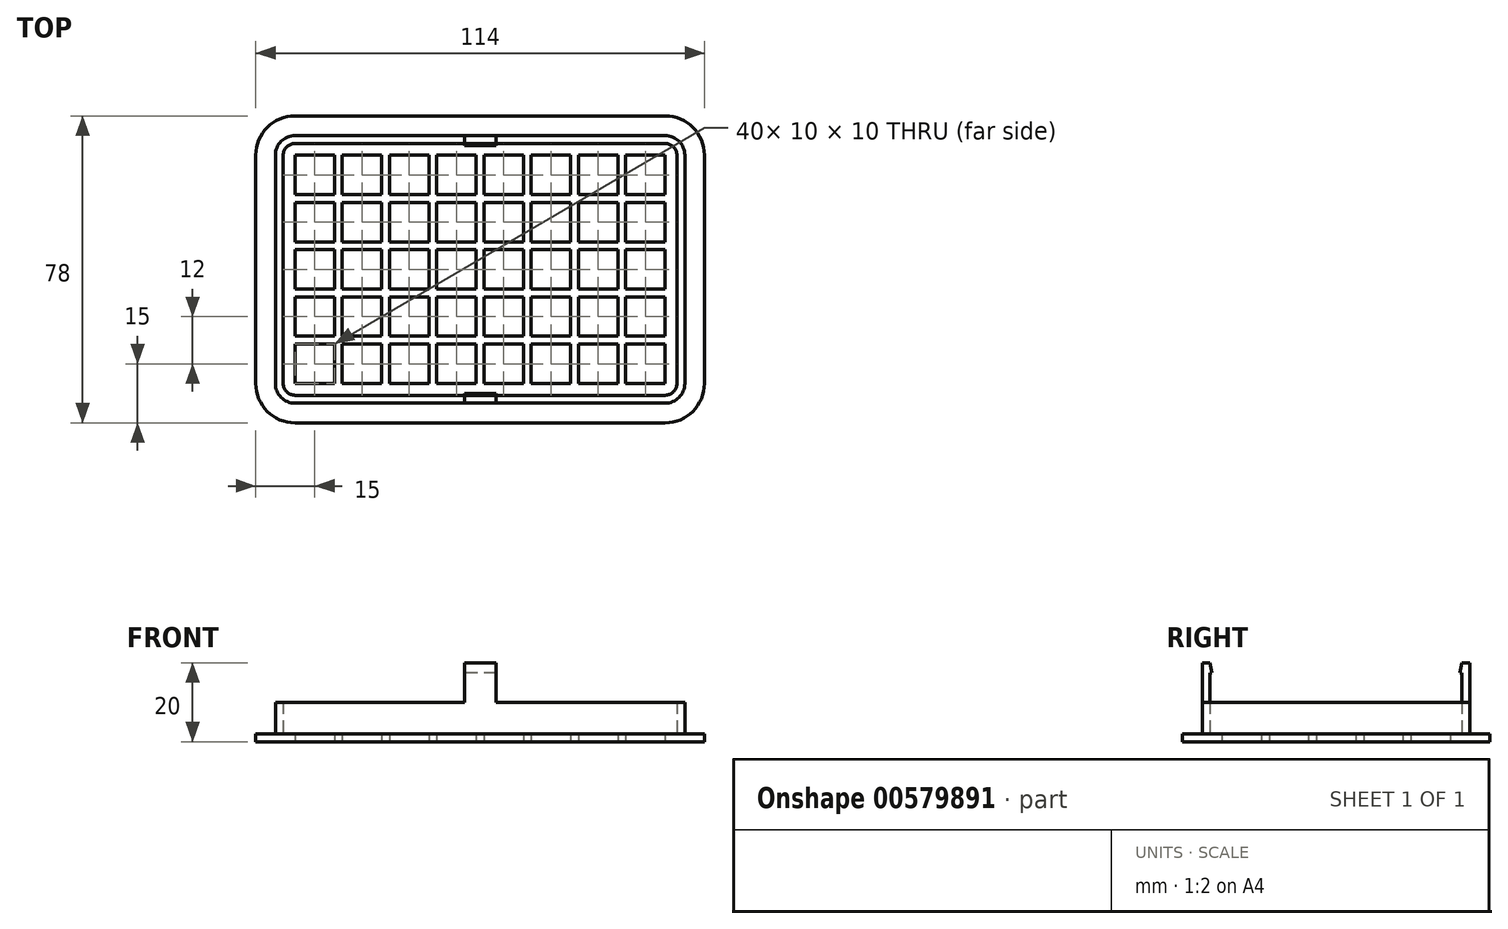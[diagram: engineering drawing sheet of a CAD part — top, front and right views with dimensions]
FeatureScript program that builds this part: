
annotation { "Feature Type Name" : "Feature", "Feature Type Description" : "" }
export const myFeature = defineFeature(function(context is Context, id is Id, definition is map)
    precondition{}
    {
        {
            var Q0;
            Q0=qCreatedBy(makeId("Top.planeOp"),FACE);
            var sketch = newSketch(context, id + "F0", { "sketchPlane" : qUnion([Q0])});
            skLineSegment(sketch, "E0.bottom", {"start": v(10, 0) * mm, "end": v(104, 0) * mm});
            skLineSegment(sketch, "E0.top", {"start": v(10, 78) * mm, "end": v(104, 78) * mm});
            skLineSegment(sketch, "E0.left", {"start": v(0, 10) * mm, "end": v(0, 68) * mm});
            skLineSegment(sketch, "E0.right", {"start": v(114, 10) * mm, "end": v(114, 68) * mm});
            skPoint(sketch, "E1.visualSharp", {"position": v(0, 78) * mm});
            skArc(sketch, "E1.filletArc", {"start": v(10, 78) * mm, "mid": v(2.93, 75.07) * mm, "end": v(0, 68) * mm});
            skPoint(sketch, "E2.visualSharp", {"position": v(114, 78) * mm});
            skArc(sketch, "E2.filletArc", {"start": v(114, 68) * mm, "mid": v(111.07, 75.07) * mm, "end": v(104, 78) * mm});
            skPoint(sketch, "E3.visualSharp", {"position": v(114, 0) * mm});
            skArc(sketch, "E3.filletArc", {"start": v(104, 0) * mm, "mid": v(111.07, 2.93) * mm, "end": v(114, 10) * mm});
            skPoint(sketch, "E4.visualSharp", {"position": v(0, 0) * mm});
            skArc(sketch, "E4.filletArc", {"start": v(0, 10) * mm, "mid": v(2.93, 2.93) * mm, "end": v(10, 0) * mm});
            skArc(sketch, "E5.0", {"start": v(5, 10) * mm, "mid": v(6.46, 6.46) * mm, "end": v(10, 5) * mm});
            skLineSegment(sketch, "E5.1", {"start": v(5, 10) * mm, "end": v(5, 68) * mm});
            skLineSegment(sketch, "E5.2", {"start": v(10, 5) * mm, "end": v(104, 5) * mm});
            skArc(sketch, "E5.3", {"start": v(10, 73) * mm, "mid": v(6.46, 71.54) * mm, "end": v(5, 68) * mm});
            skArc(sketch, "E5.4", {"start": v(104, 5) * mm, "mid": v(107.54, 6.46) * mm, "end": v(109, 10) * mm});
            skLineSegment(sketch, "E5.5", {"start": v(109, 10) * mm, "end": v(109, 68) * mm});
            skArc(sketch, "E5.6", {"start": v(109, 68) * mm, "mid": v(107.54, 71.54) * mm, "end": v(104, 73) * mm});
            skLineSegment(sketch, "E5.7", {"start": v(10, 73) * mm, "end": v(104, 73) * mm});
            skArc(sketch, "E6.0", {"start": v(7, 10) * mm, "mid": v(7.88, 7.88) * mm, "end": v(10, 7) * mm});
            skLineSegment(sketch, "E6.1", {"start": v(7, 10) * mm, "end": v(7, 68) * mm});
            skLineSegment(sketch, "E6.2", {"start": v(10, 7) * mm, "end": v(104, 7) * mm});
            skArc(sketch, "E6.3", {"start": v(10, 71) * mm, "mid": v(7.88, 70.12) * mm, "end": v(7, 68) * mm});
            skArc(sketch, "E6.4", {"start": v(104, 7) * mm, "mid": v(106.12, 7.88) * mm, "end": v(107, 10) * mm});
            skLineSegment(sketch, "E6.5", {"start": v(107, 10) * mm, "end": v(107, 68) * mm});
            skArc(sketch, "E6.6", {"start": v(107, 68) * mm, "mid": v(106.12, 70.12) * mm, "end": v(104, 71) * mm});
            skLineSegment(sketch, "E6.7", {"start": v(10, 71) * mm, "end": v(104, 71) * mm});
            skLineSegment(sketch, "E7.bottom", {"start": v(10, 68) * mm, "end": v(20, 68) * mm});
            skLineSegment(sketch, "E7.top", {"start": v(10, 58) * mm, "end": v(20, 58) * mm});
            skLineSegment(sketch, "E7.left", {"start": v(10, 68) * mm, "end": v(10, 58) * mm});
            skLineSegment(sketch, "E7.right", {"start": v(20, 68) * mm, "end": v(20, 58) * mm});
            skLineSegment(sketch, "E8.0.1.0", {"start": v(10, 46) * mm, "end": v(20, 46) * mm});
            skLineSegment(sketch, "E8.0.1.1", {"start": v(20, 56) * mm, "end": v(20, 46) * mm});
            skLineSegment(sketch, "E8.0.1.2", {"start": v(10, 56) * mm, "end": v(20, 56) * mm});
            skLineSegment(sketch, "E8.0.1.3", {"start": v(10, 56) * mm, "end": v(10, 46) * mm});
            skLineSegment(sketch, "E8.0.2.0", {"start": v(10, 34) * mm, "end": v(20, 34) * mm});
            skLineSegment(sketch, "E8.0.2.1", {"start": v(20, 44) * mm, "end": v(20, 34) * mm});
            skLineSegment(sketch, "E8.0.2.2", {"start": v(10, 44) * mm, "end": v(20, 44) * mm});
            skLineSegment(sketch, "E8.0.2.3", {"start": v(10, 44) * mm, "end": v(10, 34) * mm});
            skLineSegment(sketch, "E8.0.3.0", {"start": v(10, 22) * mm, "end": v(20, 22) * mm});
            skLineSegment(sketch, "E8.0.3.1", {"start": v(20, 32) * mm, "end": v(20, 22) * mm});
            skLineSegment(sketch, "E8.0.3.2", {"start": v(10, 32) * mm, "end": v(20, 32) * mm});
            skLineSegment(sketch, "E8.0.3.3", {"start": v(10, 32) * mm, "end": v(10, 22) * mm});
            skLineSegment(sketch, "E8.0.4.0", {"start": v(10, 10) * mm, "end": v(20, 10) * mm});
            skLineSegment(sketch, "E8.0.4.1", {"start": v(20, 20) * mm, "end": v(20, 10) * mm});
            skLineSegment(sketch, "E8.0.4.2", {"start": v(10, 20) * mm, "end": v(20, 20) * mm});
            skLineSegment(sketch, "E8.0.4.3", {"start": v(10, 20) * mm, "end": v(10, 10) * mm});
            skLineSegment(sketch, "E8.1.0.0", {"start": v(22, 58) * mm, "end": v(32, 58) * mm});
            skLineSegment(sketch, "E8.1.0.1", {"start": v(32, 68) * mm, "end": v(32, 58) * mm});
            skLineSegment(sketch, "E8.1.0.2", {"start": v(22, 68) * mm, "end": v(32, 68) * mm});
            skLineSegment(sketch, "E8.1.0.3", {"start": v(22, 68) * mm, "end": v(22, 58) * mm});
            skLineSegment(sketch, "E8.1.1.0", {"start": v(22, 46) * mm, "end": v(32, 46) * mm});
            skLineSegment(sketch, "E8.1.1.1", {"start": v(32, 56) * mm, "end": v(32, 46) * mm});
            skLineSegment(sketch, "E8.1.1.2", {"start": v(22, 56) * mm, "end": v(32, 56) * mm});
            skLineSegment(sketch, "E8.1.1.3", {"start": v(22, 56) * mm, "end": v(22, 46) * mm});
            skLineSegment(sketch, "E8.1.2.0", {"start": v(22, 34) * mm, "end": v(32, 34) * mm});
            skLineSegment(sketch, "E8.1.2.1", {"start": v(32, 44) * mm, "end": v(32, 34) * mm});
            skLineSegment(sketch, "E8.1.2.2", {"start": v(22, 44) * mm, "end": v(32, 44) * mm});
            skLineSegment(sketch, "E8.1.2.3", {"start": v(22, 44) * mm, "end": v(22, 34) * mm});
            skLineSegment(sketch, "E8.1.3.0", {"start": v(22, 22) * mm, "end": v(32, 22) * mm});
            skLineSegment(sketch, "E8.1.3.1", {"start": v(32, 32) * mm, "end": v(32, 22) * mm});
            skLineSegment(sketch, "E8.1.3.2", {"start": v(22, 32) * mm, "end": v(32, 32) * mm});
            skLineSegment(sketch, "E8.1.3.3", {"start": v(22, 32) * mm, "end": v(22, 22) * mm});
            skLineSegment(sketch, "E8.1.4.0", {"start": v(22, 10) * mm, "end": v(32, 10) * mm});
            skLineSegment(sketch, "E8.1.4.1", {"start": v(32, 20) * mm, "end": v(32, 10) * mm});
            skLineSegment(sketch, "E8.1.4.2", {"start": v(22, 20) * mm, "end": v(32, 20) * mm});
            skLineSegment(sketch, "E8.1.4.3", {"start": v(22, 20) * mm, "end": v(22, 10) * mm});
            skLineSegment(sketch, "E8.2.0.0", {"start": v(34, 58) * mm, "end": v(44, 58) * mm});
            skLineSegment(sketch, "E8.2.0.1", {"start": v(44, 68) * mm, "end": v(44, 58) * mm});
            skLineSegment(sketch, "E8.2.0.2", {"start": v(34, 68) * mm, "end": v(44, 68) * mm});
            skLineSegment(sketch, "E8.2.0.3", {"start": v(34, 68) * mm, "end": v(34, 58) * mm});
            skLineSegment(sketch, "E8.2.1.0", {"start": v(34, 46) * mm, "end": v(44, 46) * mm});
            skLineSegment(sketch, "E8.2.1.1", {"start": v(44, 56) * mm, "end": v(44, 46) * mm});
            skLineSegment(sketch, "E8.2.1.2", {"start": v(34, 56) * mm, "end": v(44, 56) * mm});
            skLineSegment(sketch, "E8.2.1.3", {"start": v(34, 56) * mm, "end": v(34, 46) * mm});
            skLineSegment(sketch, "E8.2.2.0", {"start": v(34, 34) * mm, "end": v(44, 34) * mm});
            skLineSegment(sketch, "E8.2.2.1", {"start": v(44, 44) * mm, "end": v(44, 34) * mm});
            skLineSegment(sketch, "E8.2.2.2", {"start": v(34, 44) * mm, "end": v(44, 44) * mm});
            skLineSegment(sketch, "E8.2.2.3", {"start": v(34, 44) * mm, "end": v(34, 34) * mm});
            skLineSegment(sketch, "E8.2.3.0", {"start": v(34, 22) * mm, "end": v(44, 22) * mm});
            skLineSegment(sketch, "E8.2.3.1", {"start": v(44, 32) * mm, "end": v(44, 22) * mm});
            skLineSegment(sketch, "E8.2.3.2", {"start": v(34, 32) * mm, "end": v(44, 32) * mm});
            skLineSegment(sketch, "E8.2.3.3", {"start": v(34, 32) * mm, "end": v(34, 22) * mm});
            skLineSegment(sketch, "E8.2.4.0", {"start": v(34, 10) * mm, "end": v(44, 10) * mm});
            skLineSegment(sketch, "E8.2.4.1", {"start": v(44, 20) * mm, "end": v(44, 10) * mm});
            skLineSegment(sketch, "E8.2.4.2", {"start": v(34, 20) * mm, "end": v(44, 20) * mm});
            skLineSegment(sketch, "E8.2.4.3", {"start": v(34, 20) * mm, "end": v(34, 10) * mm});
            skLineSegment(sketch, "E8.3.0.0", {"start": v(46, 58) * mm, "end": v(56, 58) * mm});
            skLineSegment(sketch, "E8.3.0.1", {"start": v(56, 68) * mm, "end": v(56, 58) * mm});
            skLineSegment(sketch, "E8.3.0.2", {"start": v(46, 68) * mm, "end": v(56, 68) * mm});
            skLineSegment(sketch, "E8.3.0.3", {"start": v(46, 68) * mm, "end": v(46, 58) * mm});
            skLineSegment(sketch, "E8.3.1.0", {"start": v(46, 46) * mm, "end": v(56, 46) * mm});
            skLineSegment(sketch, "E8.3.1.1", {"start": v(56, 56) * mm, "end": v(56, 46) * mm});
            skLineSegment(sketch, "E8.3.1.2", {"start": v(46, 56) * mm, "end": v(56, 56) * mm});
            skLineSegment(sketch, "E8.3.1.3", {"start": v(46, 56) * mm, "end": v(46, 46) * mm});
            skLineSegment(sketch, "E8.3.2.0", {"start": v(46, 34) * mm, "end": v(56, 34) * mm});
            skLineSegment(sketch, "E8.3.2.1", {"start": v(56, 44) * mm, "end": v(56, 34) * mm});
            skLineSegment(sketch, "E8.3.2.2", {"start": v(46, 44) * mm, "end": v(56, 44) * mm});
            skLineSegment(sketch, "E8.3.2.3", {"start": v(46, 44) * mm, "end": v(46, 34) * mm});
            skLineSegment(sketch, "E8.3.3.0", {"start": v(46, 22) * mm, "end": v(56, 22) * mm});
            skLineSegment(sketch, "E8.3.3.1", {"start": v(56, 32) * mm, "end": v(56, 22) * mm});
            skLineSegment(sketch, "E8.3.3.2", {"start": v(46, 32) * mm, "end": v(56, 32) * mm});
            skLineSegment(sketch, "E8.3.3.3", {"start": v(46, 32) * mm, "end": v(46, 22) * mm});
            skLineSegment(sketch, "E8.3.4.0", {"start": v(46, 10) * mm, "end": v(56, 10) * mm});
            skLineSegment(sketch, "E8.3.4.1", {"start": v(56, 20) * mm, "end": v(56, 10) * mm});
            skLineSegment(sketch, "E8.3.4.2", {"start": v(46, 20) * mm, "end": v(56, 20) * mm});
            skLineSegment(sketch, "E8.3.4.3", {"start": v(46, 20) * mm, "end": v(46, 10) * mm});
            skLineSegment(sketch, "E8.4.0.0", {"start": v(58, 58) * mm, "end": v(68, 58) * mm});
            skLineSegment(sketch, "E8.4.0.1", {"start": v(68, 68) * mm, "end": v(68, 58) * mm});
            skLineSegment(sketch, "E8.4.0.2", {"start": v(58, 68) * mm, "end": v(68, 68) * mm});
            skLineSegment(sketch, "E8.4.0.3", {"start": v(58, 68) * mm, "end": v(58, 58) * mm});
            skLineSegment(sketch, "E8.4.1.0", {"start": v(58, 46) * mm, "end": v(68, 46) * mm});
            skLineSegment(sketch, "E8.4.1.1", {"start": v(68, 56) * mm, "end": v(68, 46) * mm});
            skLineSegment(sketch, "E8.4.1.2", {"start": v(58, 56) * mm, "end": v(68, 56) * mm});
            skLineSegment(sketch, "E8.4.1.3", {"start": v(58, 56) * mm, "end": v(58, 46) * mm});
            skLineSegment(sketch, "E8.4.2.0", {"start": v(58, 34) * mm, "end": v(68, 34) * mm});
            skLineSegment(sketch, "E8.4.2.1", {"start": v(68, 44) * mm, "end": v(68, 34) * mm});
            skLineSegment(sketch, "E8.4.2.2", {"start": v(58, 44) * mm, "end": v(68, 44) * mm});
            skLineSegment(sketch, "E8.4.2.3", {"start": v(58, 44) * mm, "end": v(58, 34) * mm});
            skLineSegment(sketch, "E8.4.3.0", {"start": v(58, 22) * mm, "end": v(68, 22) * mm});
            skLineSegment(sketch, "E8.4.3.1", {"start": v(68, 32) * mm, "end": v(68, 22) * mm});
            skLineSegment(sketch, "E8.4.3.2", {"start": v(58, 32) * mm, "end": v(68, 32) * mm});
            skLineSegment(sketch, "E8.4.3.3", {"start": v(58, 32) * mm, "end": v(58, 22) * mm});
            skLineSegment(sketch, "E8.4.4.0", {"start": v(58, 10) * mm, "end": v(68, 10) * mm});
            skLineSegment(sketch, "E8.4.4.1", {"start": v(68, 20) * mm, "end": v(68, 10) * mm});
            skLineSegment(sketch, "E8.4.4.2", {"start": v(58, 20) * mm, "end": v(68, 20) * mm});
            skLineSegment(sketch, "E8.4.4.3", {"start": v(58, 20) * mm, "end": v(58, 10) * mm});
            skLineSegment(sketch, "E8.5.0.0", {"start": v(70, 58) * mm, "end": v(80, 58) * mm});
            skLineSegment(sketch, "E8.5.0.1", {"start": v(80, 68) * mm, "end": v(80, 58) * mm});
            skLineSegment(sketch, "E8.5.0.2", {"start": v(70, 68) * mm, "end": v(80, 68) * mm});
            skLineSegment(sketch, "E8.5.0.3", {"start": v(70, 68) * mm, "end": v(70, 58) * mm});
            skLineSegment(sketch, "E8.5.1.0", {"start": v(70, 46) * mm, "end": v(80, 46) * mm});
            skLineSegment(sketch, "E8.5.1.1", {"start": v(80, 56) * mm, "end": v(80, 46) * mm});
            skLineSegment(sketch, "E8.5.1.2", {"start": v(70, 56) * mm, "end": v(80, 56) * mm});
            skLineSegment(sketch, "E8.5.1.3", {"start": v(70, 56) * mm, "end": v(70, 46) * mm});
            skLineSegment(sketch, "E8.5.2.0", {"start": v(70, 34) * mm, "end": v(80, 34) * mm});
            skLineSegment(sketch, "E8.5.2.1", {"start": v(80, 44) * mm, "end": v(80, 34) * mm});
            skLineSegment(sketch, "E8.5.2.2", {"start": v(70, 44) * mm, "end": v(80, 44) * mm});
            skLineSegment(sketch, "E8.5.2.3", {"start": v(70, 44) * mm, "end": v(70, 34) * mm});
            skLineSegment(sketch, "E8.5.3.0", {"start": v(70, 22) * mm, "end": v(80, 22) * mm});
            skLineSegment(sketch, "E8.5.3.1", {"start": v(80, 32) * mm, "end": v(80, 22) * mm});
            skLineSegment(sketch, "E8.5.3.2", {"start": v(70, 32) * mm, "end": v(80, 32) * mm});
            skLineSegment(sketch, "E8.5.3.3", {"start": v(70, 32) * mm, "end": v(70, 22) * mm});
            skLineSegment(sketch, "E8.5.4.0", {"start": v(70, 10) * mm, "end": v(80, 10) * mm});
            skLineSegment(sketch, "E8.5.4.1", {"start": v(80, 20) * mm, "end": v(80, 10) * mm});
            skLineSegment(sketch, "E8.5.4.2", {"start": v(70, 20) * mm, "end": v(80, 20) * mm});
            skLineSegment(sketch, "E8.5.4.3", {"start": v(70, 20) * mm, "end": v(70, 10) * mm});
            skLineSegment(sketch, "E8.6.0.0", {"start": v(82, 58) * mm, "end": v(92, 58) * mm});
            skLineSegment(sketch, "E8.6.0.1", {"start": v(92, 68) * mm, "end": v(92, 58) * mm});
            skLineSegment(sketch, "E8.6.0.2", {"start": v(82, 68) * mm, "end": v(92, 68) * mm});
            skLineSegment(sketch, "E8.6.0.3", {"start": v(82, 68) * mm, "end": v(82, 58) * mm});
            skLineSegment(sketch, "E8.6.1.0", {"start": v(82, 46) * mm, "end": v(92, 46) * mm});
            skLineSegment(sketch, "E8.6.1.1", {"start": v(92, 56) * mm, "end": v(92, 46) * mm});
            skLineSegment(sketch, "E8.6.1.2", {"start": v(82, 56) * mm, "end": v(92, 56) * mm});
            skLineSegment(sketch, "E8.6.1.3", {"start": v(82, 56) * mm, "end": v(82, 46) * mm});
            skLineSegment(sketch, "E8.6.2.0", {"start": v(82, 34) * mm, "end": v(92, 34) * mm});
            skLineSegment(sketch, "E8.6.2.1", {"start": v(92, 44) * mm, "end": v(92, 34) * mm});
            skLineSegment(sketch, "E8.6.2.2", {"start": v(82, 44) * mm, "end": v(92, 44) * mm});
            skLineSegment(sketch, "E8.6.2.3", {"start": v(82, 44) * mm, "end": v(82, 34) * mm});
            skLineSegment(sketch, "E8.6.3.0", {"start": v(82, 22) * mm, "end": v(92, 22) * mm});
            skLineSegment(sketch, "E8.6.3.1", {"start": v(92, 32) * mm, "end": v(92, 22) * mm});
            skLineSegment(sketch, "E8.6.3.2", {"start": v(82, 32) * mm, "end": v(92, 32) * mm});
            skLineSegment(sketch, "E8.6.3.3", {"start": v(82, 32) * mm, "end": v(82, 22) * mm});
            skLineSegment(sketch, "E8.6.4.0", {"start": v(82, 10) * mm, "end": v(92, 10) * mm});
            skLineSegment(sketch, "E8.6.4.1", {"start": v(92, 20) * mm, "end": v(92, 10) * mm});
            skLineSegment(sketch, "E8.6.4.2", {"start": v(82, 20) * mm, "end": v(92, 20) * mm});
            skLineSegment(sketch, "E8.6.4.3", {"start": v(82, 20) * mm, "end": v(82, 10) * mm});
            skLineSegment(sketch, "E8.7.0.0", {"start": v(94, 58) * mm, "end": v(104, 58) * mm});
            skLineSegment(sketch, "E8.7.0.1", {"start": v(104, 68) * mm, "end": v(104, 58) * mm});
            skLineSegment(sketch, "E8.7.0.2", {"start": v(94, 68) * mm, "end": v(104, 68) * mm});
            skLineSegment(sketch, "E8.7.0.3", {"start": v(94, 68) * mm, "end": v(94, 58) * mm});
            skLineSegment(sketch, "E8.7.1.0", {"start": v(94, 46) * mm, "end": v(104, 46) * mm});
            skLineSegment(sketch, "E8.7.1.1", {"start": v(104, 56) * mm, "end": v(104, 46) * mm});
            skLineSegment(sketch, "E8.7.1.2", {"start": v(94, 56) * mm, "end": v(104, 56) * mm});
            skLineSegment(sketch, "E8.7.1.3", {"start": v(94, 56) * mm, "end": v(94, 46) * mm});
            skLineSegment(sketch, "E8.7.2.0", {"start": v(94, 34) * mm, "end": v(104, 34) * mm});
            skLineSegment(sketch, "E8.7.2.1", {"start": v(104, 44) * mm, "end": v(104, 34) * mm});
            skLineSegment(sketch, "E8.7.2.2", {"start": v(94, 44) * mm, "end": v(104, 44) * mm});
            skLineSegment(sketch, "E8.7.2.3", {"start": v(94, 44) * mm, "end": v(94, 34) * mm});
            skLineSegment(sketch, "E8.7.3.0", {"start": v(94, 22) * mm, "end": v(104, 22) * mm});
            skLineSegment(sketch, "E8.7.3.1", {"start": v(104, 32) * mm, "end": v(104, 22) * mm});
            skLineSegment(sketch, "E8.7.3.2", {"start": v(94, 32) * mm, "end": v(104, 32) * mm});
            skLineSegment(sketch, "E8.7.3.3", {"start": v(94, 32) * mm, "end": v(94, 22) * mm});
            skLineSegment(sketch, "E8.7.4.0", {"start": v(94, 10) * mm, "end": v(104, 10) * mm});
            skLineSegment(sketch, "E8.7.4.1", {"start": v(104, 20) * mm, "end": v(104, 10) * mm});
            skLineSegment(sketch, "E8.7.4.2", {"start": v(94, 20) * mm, "end": v(104, 20) * mm});
            skLineSegment(sketch, "E8.7.4.3", {"start": v(94, 20) * mm, "end": v(94, 10) * mm});
            skLineSegment(sketch, "E8.direction1", {"start": v(10, 58) * mm, "end": v(22, 58) * mm, "construction": true});
            skLineSegment(sketch, "E8.direction2", {"start": v(10, 58) * mm, "end": v(10, 46) * mm, "construction": true});
            skSolve(sketch);
        }
        {
            var Q0;
            Q0 = qSketchRegion(id + "F0", true);
            var Q1;
            Q1=makeQuery(id+"F0.imprint","IMPRINT",FACE,{"disambiguationData":[TD([[makeQuery(id+"F0.imprint","IMPRINT",EDGE,{"derivedFrom":sQuery(id+"F0.wireOp",EDGE,"E6.0")}),1.0]])]});
            var Q2;
            Q2=makeQuery(id+"F0.imprint","IMPRINT",FACE,{"disambiguationData":[TD([[makeQuery(id+"F0.imprint","IMPRINT",EDGE,{"derivedFrom":sQuery(id+"F0.wireOp",EDGE,"E5.0")}),1.0]])]});
            extrude(context, id + "F1", {"entities" : qUnion([Q0, Q1, Q2]), "depth" : 2 * mm, "offsetDistance" : 25 * mm});
        }
        {
            var Q0;
            Q0=makeQuery(id+"F0.imprint","IMPRINT",FACE,{"disambiguationData":[TD([[makeQuery(id+"F0.imprint","IMPRINT",EDGE,{"derivedFrom":sQuery(id+"F0.wireOp",EDGE,"E5.0")}),1.0]])]});
            extrude(context, id + "F2", {"entities" : qUnion([Q0]), "operationType" : NewBodyOperationType.ADD, "depth" : 10 * mm, "offsetDistance" : 25 * mm});
        }
        {
            var Q0;
            Q0=makeQuery(id+"F2.opExtrude","CAP_FACE",FACE,{"disambiguationData":[OSD([sQuery(id+"F0.wireOp",EDGE,"E5.0"),sQuery(id+"F0.wireOp",EDGE,"E5.1"),sQuery(id+"F0.wireOp",EDGE,"E5.2"),sQuery(id+"F0.wireOp",EDGE,"E5.3"),sQuery(id+"F0.wireOp",EDGE,"E5.4"),sQuery(id+"F0.wireOp",EDGE,"E5.5"),sQuery(id+"F0.wireOp",EDGE,"E5.6"),sQuery(id+"F0.wireOp",EDGE,"E5.7"),sQuery(id+"F0.wireOp",EDGE,"E6.0"),sQuery(id+"F0.wireOp",EDGE,"E6.1"),sQuery(id+"F0.wireOp",EDGE,"E6.2"),sQuery(id+"F0.wireOp",EDGE,"E6.3"),sQuery(id+"F0.wireOp",EDGE,"E6.4"),sQuery(id+"F0.wireOp",EDGE,"E6.5"),sQuery(id+"F0.wireOp",EDGE,"E6.6"),sQuery(id+"F0.wireOp",EDGE,"E6.7")])],"isStart":false});
            var sketch = newSketch(context, id + "F3", { "sketchPlane" : qUnion([Q0])});
            skLineSegment(sketch, "E9.0.0", {"start": v(61, 73) * mm, "end": v(53, 73) * mm});
            skLineSegment(sketch, "E9.0.4", {"start": v(53, 5) * mm, "end": v(61, 5) * mm});
            skLineSegment(sketch, "E10.0", {"start": v(53, 71) * mm, "end": v(61, 71) * mm});
            skLineSegment(sketch, "E11.0", {"start": v(53, 7) * mm, "end": v(61, 7) * mm});
            skLineSegment(sketch, "E12", {"start": v(57, 73) * mm, "end": v(57, 5) * mm, "construction": true});
            skLineSegment(sketch, "E13", {"start": v(5, 39) * mm, "end": v(109, 39) * mm, "construction": true});
            skLineSegment(sketch, "E14", {"start": v(53, 73) * mm, "end": v(53, 71) * mm});
            skLineSegment(sketch, "E15.MirrorCS", {"start": v(61, 73) * mm, "end": v(61, 71) * mm});
            skPoint(sketch, "E16.orphan", {"position": v(10, 71) * mm});
            skPoint(sketch, "E9.0.1.start.orphan", {"position": v(10, 73) * mm});
            skPoint(sketch, "E17.orphan", {"position": v(104, 71) * mm});
            skLineSegment(sketch, "E18.MirrorCS", {"start": v(61, 5) * mm, "end": v(61, 7) * mm});
            skLineSegment(sketch, "E19.MirrorCS", {"start": v(53, 5) * mm, "end": v(53, 7) * mm});
            skLineSegment(sketch, "E20.MirrorCS", {"start": v(61, 5) * mm, "end": v(53, 5) * mm});
            skPoint(sketch, "E21.orphan", {"position": v(10, 7) * mm});
            skPoint(sketch, "E22.orphan", {"position": v(104, 7) * mm});
            skPoint(sketch, "E9.0.5.start.orphan", {"position": v(104, 5) * mm});
            skPoint(sketch, "E23.orphan", {"position": v(109, 10) * mm});
            skPoint(sketch, "E9.0.7.end.orphan", {"position": v(104, 73) * mm});
            skPoint(sketch, "E9.0.7.start.orphan", {"position": v(109, 68) * mm});
            skPoint(sketch, "E24.orphan", {"position": v(5, 68) * mm});
            skPoint(sketch, "E9.0.3.end.orphan", {"position": v(10, 5) * mm});
            skPoint(sketch, "E9.0.3.start.orphan", {"position": v(5, 10) * mm});
            skSolve(sketch);
        }
        {
            var Q0;
            Q0 = qSketchRegion(id + "F3", true);
            extrude(context, id + "F4", {"entities" : qUnion([Q0]), "operationType" : NewBodyOperationType.ADD, "depth" : 10 * mm, "offsetDistance" : 25 * mm});
        }
        {
            var Q0;
            Q0=makeQuery(id+"F4.opExtrude","SWEPT_FACE",FACE,{"disambiguationData":[OSD([sQuery(id+"F3.wireOp",EDGE,"E14")])]});
            var sketch = newSketch(context, id + "F5", { "sketchPlane" : qUnion([Q0])});
            skLineSegment(sketch, "E25", {"start": v(-71, 20) * mm, "end": v(-70.5, 17.5) * mm});
            skLineSegment(sketch, "E26", {"start": v(-70.5, 17.5) * mm, "end": v(-71, 17.5) * mm});
            skPoint(sketch, "E27.0", {"position": v(-39, 10) * mm});
            skLineSegment(sketch, "E28", {"start": v(-39, 10) * mm, "end": v(-39, 33.3) * mm, "construction": true});
            skLineSegment(sketch, "E29", {"start": v(-71, 17.5) * mm, "end": v(-71, 20) * mm});
            skLineSegment(sketch, "E30.MirrorCS", {"start": v(-7.5, 17.5) * mm, "end": v(-7, 17.5) * mm});
            skLineSegment(sketch, "E31.MirrorCS", {"start": v(-7, 20) * mm, "end": v(-7.5, 17.5) * mm});
            skLineSegment(sketch, "E32.MirrorCS", {"start": v(-7, 17.5) * mm, "end": v(-7, 20) * mm});
            skSolve(sketch);
        }
        {
            var Q0;
            Q0 = qSketchRegion(id + "F5", true);
            var Q1;
            Q1=makeQuery(id+"F4.opExtrude","SWEPT_FACE",FACE,{"disambiguationData":[OSD([sQuery(id+"F3.wireOp",EDGE,"E15.MirrorCS")])]});
            extrude(context, id + "F6", {"entities" : qUnion([Q0]), "operationType" : NewBodyOperationType.ADD, "endBound" : BoundingType.UP_TO_SURFACE, "oppositeDirection" : true, "depth" : 25 * mm, "endBoundEntityFace" : qUnion([Q1]), "offsetDistance" : 25 * mm});
        }
    });
